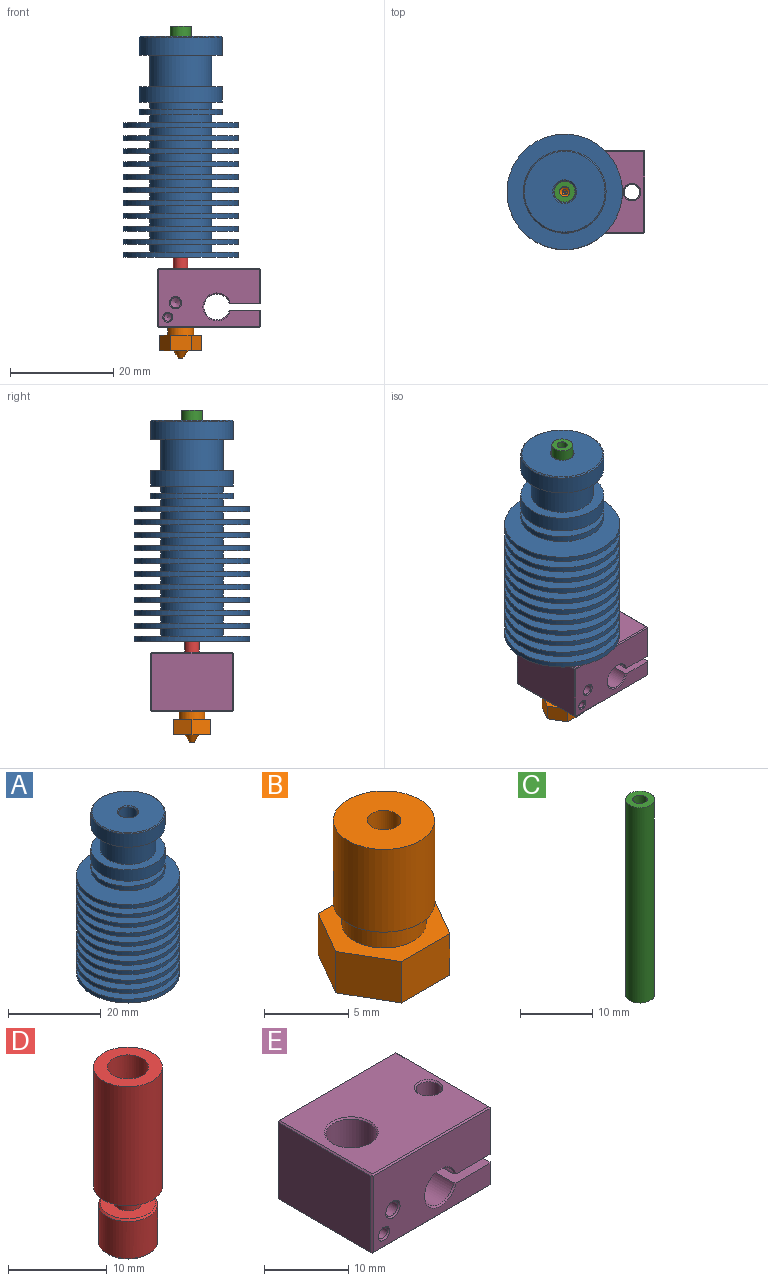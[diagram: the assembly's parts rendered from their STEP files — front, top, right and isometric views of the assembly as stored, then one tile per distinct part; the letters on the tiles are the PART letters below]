
ASSEMBLY  parts=5 mates=4
PART A: 62 faces, bbox 22.3x22.3x42.7 mm
  f0: cone r=0mm half-angle=59deg, axis (0,0,-1), area 26.3mm2, adj f57,f59
  f1: plane 15.6x15.6mm, normal (0,0,1), area 174.5mm2, adj f58,f61
  f2: plane 22.3x22.3mm, normal (0,0,-1), area 347.6mm2, adj f3,f60
  f3: cylinder r=11.15mm len=22.3mm, axis (0,0,1), area 70.1mm2, adj f2,f4
  f4: plane 22.3x22.3mm, normal (0,0,1), area 277.5mm2, adj f3,f5
  f5: cylinder r=6mm len=12mm, axis (0,0,1), area 56.5mm2, adj f4,f6
  f6: plane 22.3x22.3mm, normal (0,0,-1), area 277.5mm2, adj f5,f7
  f7: cylinder r=11.15mm len=22.3mm, axis (0,0,1), area 70.1mm2, adj f6,f8
  f8: plane 22.3x22.3mm, normal (0,0,1), area 277.5mm2, adj f7,f9
  f9: cylinder r=6mm len=12mm, axis (0,0,1), area 56.5mm2, adj f8,f10
  f10: plane 22.3x22.3mm, normal (0,0,-1), area 277.5mm2, adj f9,f11
  f11: cylinder r=11.15mm len=22.3mm, axis (0,0,1), area 70.1mm2, adj f10,f12
  f12: plane 22.3x22.3mm, normal (0,0,1), area 277.5mm2, adj f11,f13
  f13: cylinder r=6mm len=12mm, axis (0,0,1), area 56.5mm2, adj f12,f14
  f14: plane 22.3x22.3mm, normal (0,0,-1), area 277.5mm2, adj f13,f15
  f15: cylinder r=11.15mm len=22.3mm, axis (0,0,1), area 70.1mm2, adj f14,f16
  f16: plane 22.3x22.3mm, normal (0,0,1), area 277.5mm2, adj f15,f17
  f17: cylinder r=6mm len=12mm, axis (0,0,1), area 56.5mm2, adj f16,f18
  f18: plane 22.3x22.3mm, normal (0,0,-1), area 277.5mm2, adj f17,f19
  f19: cylinder r=11.15mm len=22.3mm, axis (0,0,1), area 70.1mm2, adj f18,f20
  f20: plane 22.3x22.3mm, normal (0,0,1), area 277.5mm2, adj f19,f21
  f21: cylinder r=6mm len=12mm, axis (0,0,1), area 56.5mm2, adj f20,f22
  f22: plane 22.3x22.3mm, normal (0,0,-1), area 277.5mm2, adj f21,f23
  f23: cylinder r=11.15mm len=22.3mm, axis (0,0,1), area 70.1mm2, adj f22,f24
  f24: plane 22.3x22.3mm, normal (0,0,1), area 277.5mm2, adj f23,f25
  f25: cylinder r=6mm len=12mm, axis (0,0,1), area 56.5mm2, adj f24,f26
  f26: plane 22.3x22.3mm, normal (0,0,-1), area 277.5mm2, adj f25,f27
  f27: cylinder r=11.15mm len=22.3mm, axis (0,0,1), area 70.1mm2, adj f26,f28
  f28: plane 22.3x22.3mm, normal (0,0,1), area 277.5mm2, adj f27,f29
  f29: cylinder r=6mm len=12mm, axis (0,0,1), area 56.5mm2, adj f28,f30
  f30: plane 22.3x22.3mm, normal (0,0,-1), area 277.5mm2, adj f29,f31
  f31: cylinder r=11.15mm len=22.3mm, axis (0,0,1), area 70.1mm2, adj f30,f32
  f32: plane 22.3x22.3mm, normal (0,0,1), area 277.5mm2, adj f31,f33
  f33: cylinder r=6mm len=12mm, axis (0,0,1), area 56.5mm2, adj f32,f34
  f34: plane 22.3x22.3mm, normal (0,0,-1), area 277.5mm2, adj f33,f35
  f35: cylinder r=11.15mm len=22.3mm, axis (0,0,1), area 70.1mm2, adj f34,f36
  f36: plane 22.3x22.3mm, normal (0,0,1), area 277.5mm2, adj f35,f37
  f37: cylinder r=6mm len=12mm, axis (0,0,1), area 56.5mm2, adj f36,f38
  f38: plane 22.3x22.3mm, normal (0,0,-1), area 277.5mm2, adj f37,f39
  f39: cylinder r=11.15mm len=22.3mm, axis (0,0,1), area 70.1mm2, adj f38,f40
  f40: plane 22.3x22.3mm, normal (0,0,1), area 277.5mm2, adj f39,f41
  f41: cylinder r=6mm len=12mm, axis (0,0,1), area 56.5mm2, adj f40,f42
  f42: plane 22.3x22.3mm, normal (0,0,-1), area 277.5mm2, adj f41,f43
  f43: cylinder r=11.15mm len=22.3mm, axis (0,0,1), area 70.1mm2, adj f42,f44
  f44: plane 22.3x22.3mm, normal (0,0,1), area 277.5mm2, adj f43,f45
  f45: cylinder r=6mm len=12mm, axis (0,0,1), area 56.5mm2, adj f44,f46
  f46: plane 16x16mm, normal (0,0,-1), area 88mm2, adj f45,f47
  f47: cylinder r=8mm len=16mm, axis (0,0,1), area 57.8mm2, adj f46,f48
  f48: plane 16x16mm, normal (0,0,1), area 88mm2, adj f47,f49
  f49: cylinder r=6mm len=12mm, axis (0,0,1), area 50.9mm2, adj f48,f50
  f50: plane 16x16mm, normal (0,0,-1), area 88mm2, adj f49,f51
  f51: cylinder r=8mm len=16mm, axis (0,0,1), area 150.8mm2, adj f50,f52
  f52: plane 16x16mm, normal (0,0,1), area 88mm2, adj f51,f53
  f53: cylinder r=6mm len=12mm, axis (0,0,1), area 226.2mm2, adj f52,f54
  f54: plane 16x16mm, normal (0,0,-1), area 88mm2, adj f53,f55
  f55: cylinder r=8mm len=16mm, axis (0,0,1), area 175.9mm2, adj f54,f61
  f56: cylinder r=3.5mm len=14.49mm, axis (0,0,-1), area 318.6mm2, adj f59,f60
  f57: cylinder r=2.1mm len=26.86mm, axis (0,0,1), area 354.4mm2, adj f0,f58
  f58: cone r=2.1mm half-angle=45deg, axis (0,0,1), area 3.9mm2, adj f1,f57
  f59: cone r=3.4mm half-angle=29.5deg, axis (0,0,-1), area 4.3mm2, adj f0,f56
  f60: cone r=3.5mm half-angle=45deg, axis (0,0,-1), area 6.4mm2, adj f2,f56
  f61: cone r=7.8mm half-angle=45deg, axis (0,0,-1), area 14mm2, adj f1,f55
PART B: 19 faces, bbox 8.1x7x11.9 mm
  f0: cone r=0mm half-angle=59deg, axis (0,0,1), area 0.8mm2, adj f17,f18
  f1: cone r=0mm half-angle=59deg, axis (0,0,1), area 2.7mm2, adj f16,f17
  f2: cylinder r=2.5mm len=5mm, axis (0,0,-1), area 23.6mm2, adj f4,f12
  f3: plane 6x6mm, normal (0,0,1), area 25.1mm2, adj f5,f16
  f4: plane 6x6mm, normal (0,0,-1), area 8.6mm2, adj f2,f5
  f5: cylinder r=3mm len=6mm, axis (0,0,-1), area 113.1mm2, adj f3,f4
  f6: plane 4.04x3mm, normal (0,-1,0), area 12.1mm2, adj f7,f11,f12,f15
  f7: plane 3.5x3mm, normal (-0.87,-0.5,0), area 12.1mm2, adj f6,f8,f12,f15
  f8: plane 3.5x3mm, normal (-0.87,0.5,0), area 12.1mm2, adj f7,f9,f12,f15
  f9: plane 4.04x3mm, normal (0,1,0), area 12.1mm2, adj f8,f10,f12,f15
  f10: plane 3.5x3mm, normal (0.87,0.5,0), area 12.1mm2, adj f9,f11,f12,f15
  f11: plane 3.5x3mm, normal (0.87,-0.5,0), area 12.1mm2, adj f6,f10,f12,f15
  f12: plane 8.08x7mm, normal (0,0,1), area 22.8mm2, adj f2,f6,f7,f8,f9,f10,f11
  f13: plane 0.88x0.88mm, normal (0,0,-1), area 0.5mm2, adj f14,f18
  f14: cone r=1.4mm half-angle=35deg, axis (0,0,1), area 9.7mm2, adj f13,f15
  f15: plane 8.08x7mm, normal (0,0,-1), area 36.3mm2, adj f6,f7,f8,f9,f10,f11,f14
  f16: cylinder r=1mm len=10.5mm, axis (0,0,1), area 66mm2, adj f1,f3
  f17: cylinder r=0.5mm len=1mm, axis (0,0,1), area 2.2mm2, adj f0,f1
  f18: cylinder r=0.17mm len=0.35mm, axis (0,0,1), area 0.2mm2, adj f0,f13
PART C: 4 faces, bbox 4x4x33 mm
  f0: plane 4x4mm, normal (0,0,1), area 9.4mm2, adj f1,f3
  f1: cylinder r=1mm len=33mm, axis (0,0,1), area 207.3mm2, adj f0,f2
  f2: plane 4x4mm, normal (0,0,-1), area 9.4mm2, adj f1,f3
  f3: cylinder r=2mm len=33mm, axis (0,0,1), area 414.7mm2, adj f0,f2
PART D: 13 faces, bbox 7x7x21.9 mm
  f0: cylinder r=1mm len=17.94mm, axis (0,0,1), area 112.7mm2, adj f9,f10
  f1: plane 7x7mm, normal (0,0,1), area 24.6mm2, adj f7,f8
  f2: plane 5.6x5.6mm, normal (0,0,-1), area 20.1mm2, adj f10,f11
  f3: cylinder r=3mm len=6mm, axis (0,0,-1), area 86.7mm2, adj f11,f12
  f4: plane 5.6x5.6mm, normal (0,0,1), area 18.5mm2, adj f5,f12
  f5: cylinder r=1.4mm len=2.8mm, axis (0,0,-1), area 18.5mm2, adj f4,f6
  f6: plane 7x7mm, normal (0,0,-1), area 32.3mm2, adj f5,f7
  f7: cylinder r=3.5mm len=14.8mm, axis (0,0,-1), area 325.5mm2, adj f1,f6
  f8: cylinder r=2.1mm len=4.2mm, axis (0,0,1), area 40.9mm2, adj f1,f9
  f9: cone r=0mm half-angle=59deg, axis (0,0,1), area 12.5mm2, adj f0,f8
  f10: cone r=1mm half-angle=45deg, axis (0,0,-1), area 2mm2, adj f0,f2
  f11: cone r=2.8mm half-angle=45deg, axis (0,0,1), area 5.2mm2, adj f2,f3
  f12: cone r=3mm half-angle=45deg, axis (0,0,-1), area 5.2mm2, adj f3,f4
PART E: 45 faces, bbox 20x16x11.5 mm
  f0: plane 15.8x3.15mm, normal (1,0,0), area 49.8mm2, adj f6,f16,f31,f36
  f1: plane 19.6x11.1mm, normal (0,-1,0), area 180mm2, adj f15,f16,f17,f23,f24,f25,f30,f31
  f2: cylinder r=1.5mm len=3.15mm, axis (0,0,1), area 29.7mm2, adj f16,f19
  f3: cylinder r=2.5mm len=15.6mm, axis (0,-1,0), area 224.5mm2, adj f15,f16,f20,f23
  f4: plane 15.6x11.1mm, normal (-1,0,0), area 173.2mm2, adj f33,f38,f41,f44
  f5: plane 15.6x6.65mm, normal (1,0,0), area 103.7mm2, adj f15,f25,f26,f27
  f6: plane 19.8x11.1mm, normal (0,1,0), area 188mm2, adj f0,f15,f16,f20,f26,f32,f40,f41
  f7: plane 19.6x15.6mm, normal (0,0,-1), area 264.5mm2, adj f18,f19,f36,f39,f40,f44
  f8: plane 19.6x15.6mm, normal (0,0,1), area 264.5mm2, adj f21,f22,f27,f30,f32,f33
  f9: cylinder r=3mm len=11.1mm, axis (0,0,1), area 209.2mm2, adj f18,f21
  f10: cylinder r=1.5mm len=6.65mm, axis (0,0,1), area 62.7mm2, adj f15,f22
  f11: cone r=0mm half-angle=59deg, axis (0,-1,0), area 2.1mm2, adj f12
  f12: cylinder r=0.75mm len=4.3mm, axis (0,-1,0), area 20.3mm2, adj f11,f24
  f13: cone r=0mm half-angle=59deg, axis (0,-1,0), area 3.7mm2, adj f14
  f14: cylinder r=1mm len=2mm, axis (0,-1,0), area 11.3mm2, adj f13,f17
  f15: plane 16x6.09mm, normal (0,0,-1), area 90.2mm2, adj f1,f3,f5,f6,f10,f20,f23,f25
  f16: plane 16x6.09mm, normal (0,0,1), area 90.2mm2, adj f0,f1,f2,f3,f6,f20,f23,f31
  f17: cone r=1mm half-angle=45deg, axis (0,-1,0), area 2mm2, adj f1,f14
  f18: cone r=3mm half-angle=45deg, axis (0,0,-1), area 5.5mm2, adj f7,f9
  f19: cone r=1.5mm half-angle=45deg, axis (0,0,-1), area 2.8mm2, adj f2,f7
  f20: cone r=2.5mm half-angle=45deg, axis (0,1,0), area 4.2mm2, adj f3,f6,f15,f16
  f21: cone r=3mm half-angle=45deg, axis (0,0,1), area 5.5mm2, adj f8,f9
  f22: cone r=1.5mm half-angle=45deg, axis (0,0,1), area 2.8mm2, adj f8,f10
  f23: cone r=2.5mm half-angle=45deg, axis (0,-1,0), area 4.2mm2, adj f1,f3,f15,f16
  f24: cone r=0.75mm half-angle=45deg, axis (0,-1,0), area 1.5mm2, adj f1,f12
  f25: plane 6.65x0.2mm, normal (0.71,-0.71,0), area 1.9mm2, adj f1,f5,f15,f28
  f26: plane 6.65x0.2mm, normal (0.71,0.71,0), area 1.9mm2, adj f5,f6,f15,f29
  f27: plane 15.6x0.2mm, normal (0.71,0,0.71), area 4.4mm2, adj f5,f8,f28,f29
  f28: plane 0.2x0.2mm, normal (0.58,-0.58,0.58), area 0mm2, adj f25,f27,f30
  f29: plane 0.2x0.2mm, normal (0.58,0.58,0.58), area 0mm2, adj f26,f27,f32
  f30: plane 19.6x0.2mm, normal (0,-0.71,0.71), area 5.5mm2, adj f1,f8,f28,f34
  f31: plane 3.15x0.2mm, normal (0.71,-0.71,0), area 0.9mm2, adj f0,f1,f16,f35
  f32: plane 19.6x0.2mm, normal (0,0.71,0.71), area 5.5mm2, adj f6,f8,f29,f37
  f33: plane 15.6x0.2mm, normal (-0.71,0,0.71), area 4.4mm2, adj f4,f8,f34,f37
  f34: plane 0.2x0.2mm, normal (-0.58,-0.58,0.58), area 0mm2, adj f30,f33,f38
  f35: plane 0.2x0.2mm, normal (0.58,-0.58,-0.58), area 0mm2, adj f31,f36,f39
  f36: plane 15.8x0.2mm, normal (0.71,0,-0.71), area 4.4mm2, adj f0,f7,f35,f40
  f37: plane 0.2x0.2mm, normal (-0.58,0.58,0.58), area 0mm2, adj f32,f33,f41
  f38: plane 11.1x0.2mm, normal (-0.71,-0.71,0), area 3.1mm2, adj f1,f4,f34,f42
  f39: plane 19.6x0.2mm, normal (0,-0.71,-0.71), area 5.5mm2, adj f1,f7,f35,f42
  f40: plane 19.8x0.2mm, normal (0,0.71,-0.71), area 5.6mm2, adj f6,f7,f36,f43
  f41: plane 11.1x0.2mm, normal (-0.71,0.71,0), area 3.1mm2, adj f4,f6,f37,f43
  f42: plane 0.2x0.2mm, normal (-0.58,-0.58,-0.58), area 0mm2, adj f38,f39,f44
  f43: plane 0.2x0.2mm, normal (-0.58,0.58,-0.58), area 0mm2, adj f40,f41,f44
  f44: plane 15.6x0.2mm, normal (-0.71,0,-0.71), area 4.4mm2, adj f4,f7,f42,f43
PLACE A at identity
PLACE B t=(0,0,-0.5)mm
PLACE C at identity
PLACE D at identity
PLACE E at identity
MATE fastened D.f0 <-> A.f0  axis (0,0,-1) through (0,0,-21.35)mm
MATE fastened C.f1 <-> D.f0  axis (0,0,1) through (0,0,-9.65)mm
MATE fastened B.f0 <-> E.f9  axis (0,0,-1) through (0,0,-34.95)mm
MATE fastened E.f9 <-> D.f0  axis (0,0,1) through (0,0,-23.45)mm
